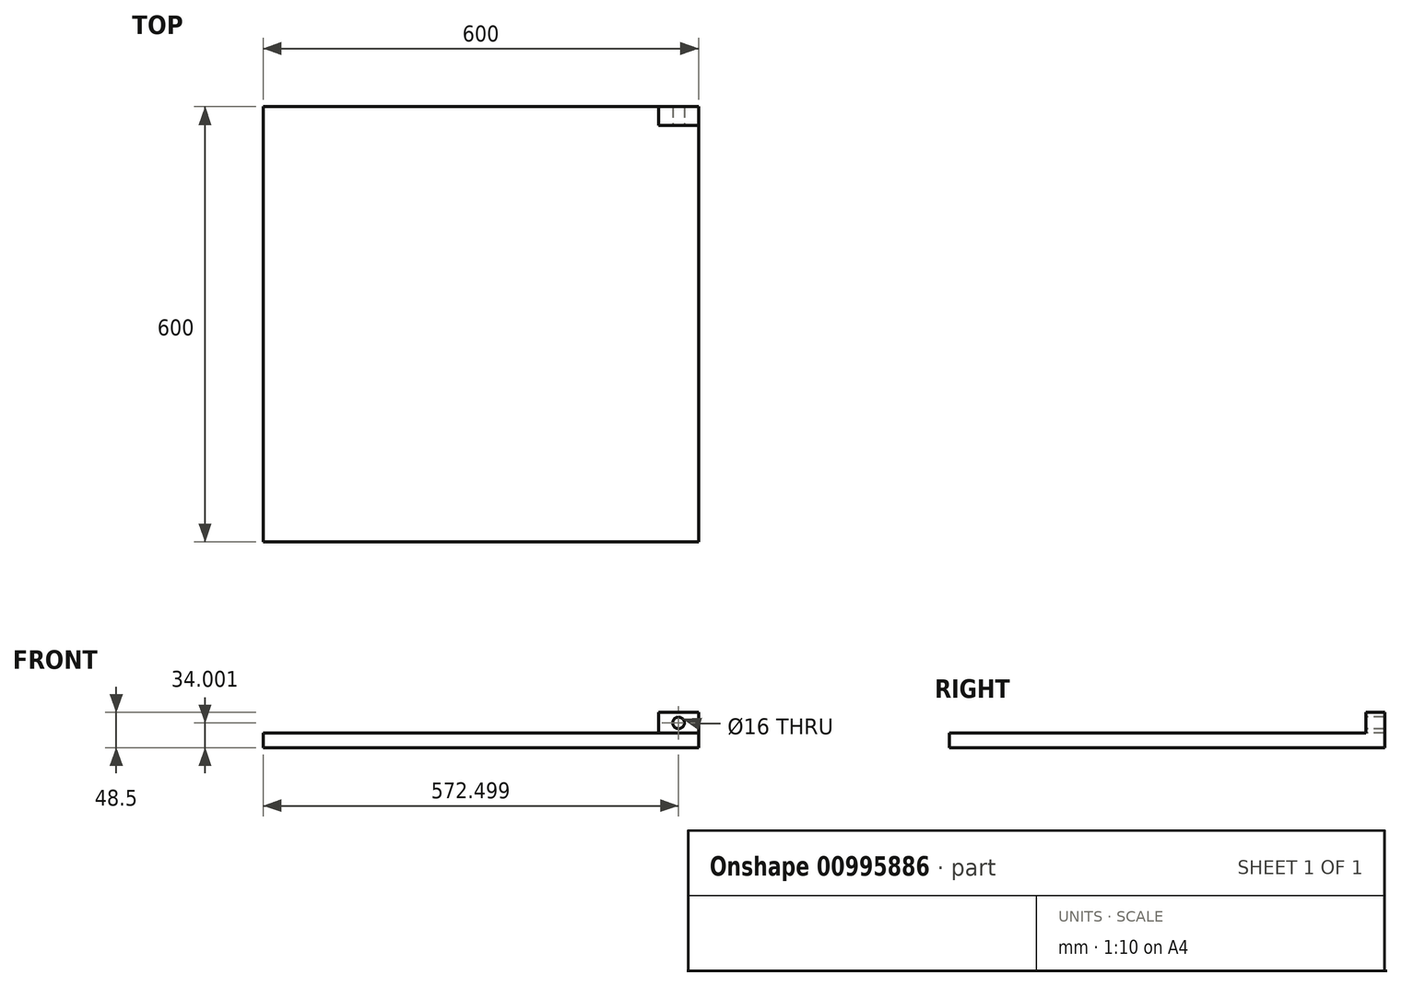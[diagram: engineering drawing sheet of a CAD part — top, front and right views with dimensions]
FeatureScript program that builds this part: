
annotation { "Feature Type Name" : "Feature", "Feature Type Description" : "" }
export const myFeature = defineFeature(function(context is Context, id is Id, definition is map)
    precondition{}
    {
        {
            var Q0;
            Q0=qCreatedBy(makeId("Front.planeOp"),FACE);
            var sketch = newSketch(context, id + "F0", { "sketchPlane" : qUnion([Q0])});
            skLineSegment(sketch, "E0.bottom", {"start": v(-302.31, 0) * mm, "end": v(297.69, 0) * mm});
            skLineSegment(sketch, "E0.top", {"start": v(-302.31, 20) * mm, "end": v(297.69, 20) * mm});
            skLineSegment(sketch, "E0.left", {"start": v(-302.31, 0) * mm, "end": v(-302.31, 20) * mm});
            skLineSegment(sketch, "E0.right", {"start": v(297.69, 0) * mm, "end": v(297.69, 20) * mm});
            skSolve(sketch);
        }
        {
            var Q0;
            Q0 = qSketchRegion(id + "F0", true);
            extrude(context, id + "F1", {"entities" : qUnion([Q0]), "depth" : 600 * mm, "offsetDistance" : 25 * mm});
        }
        {
            var Q0;
            Q0=makeQuery(id+"F1.opExtrude","SWEPT_FACE",FACE,{"disambiguationData":[OSD([sQuery(id+"F0.wireOp",EDGE,"E0.top")])]});
            var sketch = newSketch(context, id + "F2", { "sketchPlane" : qUnion([Q0])});
            skLineSegment(sketch, "E1.bottom", {"start": v(297.69, 0) * mm, "end": v(242.69, 0) * mm});
            skLineSegment(sketch, "E1.top", {"start": v(297.69, -26) * mm, "end": v(242.69, -26) * mm});
            skLineSegment(sketch, "E1.left", {"start": v(297.69, 0) * mm, "end": v(297.69, -26) * mm});
            skLineSegment(sketch, "E1.right", {"start": v(242.69, 0) * mm, "end": v(242.69, -26) * mm});
            skSolve(sketch);
        }
        {
            var Q0;
            Q0 = qSketchRegion(id + "F2", true);
            var Q1;
            Q1=makeQuery(id+"F2.imprint","IMPRINT",FACE,{"disambiguationData":[TD([[makeQuery(id+"F2.imprint","IMPRINT",EDGE,{"derivedFrom":sQuery(id+"F2.wireOp",EDGE,"E1.bottom")}),-1.0]])]});
            extrude(context, id + "F3", {"entities" : qUnion([Q0, Q1]), "operationType" : NewBodyOperationType.ADD, "depth" : 28.5 * mm, "offsetDistance" : 25 * mm});
        }
        {
            var Q0;
            Q0=makeQuery(id+"F3.opExtrude","SWEPT_FACE",FACE,{"disambiguationData":[OSD([sQuery(id+"F2.wireOp",EDGE,"E1.top")])]});
            var sketch = newSketch(context, id + "F4", { "sketchPlane" : qUnion([Q0])});
            skCircle(sketch, "E2", {"center": v(270.19, 34) * mm, "radius": 8 * mm});
            skSolve(sketch);
        }
        {
            var Q0;
            Q0=makeQuery(id+"F4.imprint","IMPRINT",FACE,{"disambiguationData":[TD([[makeQuery(id+"F4.imprint","IMPRINT",EDGE,{"derivedFrom":sQuery(id+"F4.wireOp",EDGE,"E2")}),1.0]])]});
            extrude(context, id + "F5", {"entities" : qUnion([Q0]), "operationType" : NewBodyOperationType.REMOVE, "endBound" : BoundingType.UP_TO_NEXT, "oppositeDirection" : true, "depth" : 25 * mm, "offsetDistance" : 25 * mm});
        }
    });
